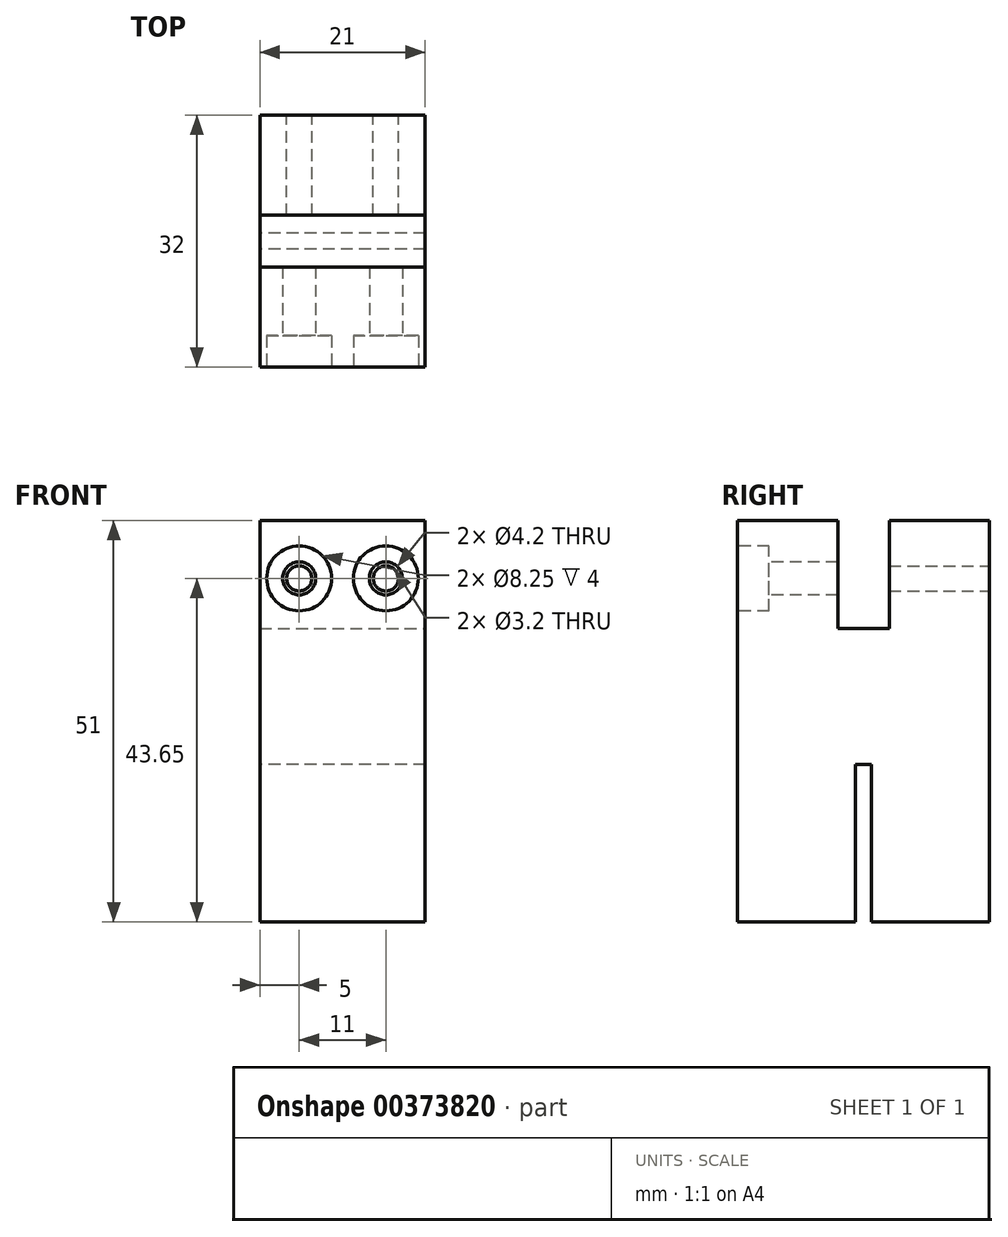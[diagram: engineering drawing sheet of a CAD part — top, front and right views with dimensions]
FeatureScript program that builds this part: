
annotation { "Feature Type Name" : "Feature", "Feature Type Description" : "" }
export const myFeature = defineFeature(function(context is Context, id is Id, definition is map)
    precondition{}
    {
        {
            var Q0;
            Q0=qCreatedBy(makeId("Right.planeOp"),FACE);
            var sketch = newSketch(context, id + "F0", { "sketchPlane" : qUnion([Q0])});
            skLineSegment(sketch, "E0.bottom", {"start": v(-16, -25) * mm, "end": v(16, -25) * mm});
            skLineSegment(sketch, "E0.top", {"start": v(-16, 25) * mm, "end": v(16, 25) * mm});
            skLineSegment(sketch, "E0.left", {"start": v(-16, -25) * mm, "end": v(-16, 25) * mm});
            skLineSegment(sketch, "E0.right", {"start": v(16, -25) * mm, "end": v(16, 25) * mm});
            skPoint(sketch, "E0.middle", {"position": v(0, 0) * mm});
            skLineSegment(sketch, "E1.bottom", {"start": v(-1, -5) * mm, "end": v(1, -5) * mm});
            skLineSegment(sketch, "E1.top", {"start": v(-1, -45) * mm, "end": v(1, -45) * mm});
            skLineSegment(sketch, "E1.left", {"start": v(-1, -5) * mm, "end": v(-1, -45) * mm});
            skLineSegment(sketch, "E1.right", {"start": v(1, -5) * mm, "end": v(1, -45) * mm});
            skPoint(sketch, "E1.middle", {"position": v(0, -25) * mm});
            skSolve(sketch);
        }
        {
            var Q0;
            Q0=makeQuery(id+"F0.imprint","IMPRINT",FACE,{"disambiguationData":[TD([[makeQuery(id+"F0.imprint","IMPRINT",EDGE,{"derivedFrom":sQuery(id+"F0.wireOp",EDGE,"E0.top")}),-1.0]])]});
            extrude(context, id + "F1", {"entities" : qUnion([Q0]), "depth" : 21 * mm});
        }
        {
            var Q0;
            Q0=makeQuery(id+"F1.opExtrude","SWEPT_FACE",FACE,{"disambiguationData":[OSD([sQuery(id+"F0.wireOp",EDGE,"E0.left")])]});
            var sketch = newSketch(context, id + "F2", { "sketchPlane" : qUnion([Q0])});
            skPoint(sketch, "E2", {"position": v(16, 18.65) * mm});
            skPoint(sketch, "E3", {"position": v(5, 18.65) * mm});
            skSolve(sketch);
        }
        {
            var Q0;
            Q0=makeQuery(id+"F1.opExtrude","CAP_FACE",FACE,{"disambiguationData":[OSD([sQuery(id+"F0.wireOp",EDGE,"E0.bottom"),sQuery(id+"F0.wireOp",EDGE,"E0.top"),sQuery(id+"F0.wireOp",EDGE,"E0.left"),sQuery(id+"F0.wireOp",EDGE,"E0.right"),sQuery(id+"F0.wireOp",EDGE,"E1.bottom"),sQuery(id+"F0.wireOp",EDGE,"E1.left"),sQuery(id+"F0.wireOp",EDGE,"E1.right")])],"isStart":false});
            var sketch = newSketch(context, id + "F3", { "sketchPlane" : qUnion([Q0])});
            skLineSegment(sketch, "E4.bottom", {"start": v(-3.28, 25) * mm, "end": v(3.27, 25) * mm});
            skLineSegment(sketch, "E4.top", {"start": v(-3.28, 12.3) * mm, "end": v(3.27, 12.3) * mm});
            skLineSegment(sketch, "E4.left", {"start": v(-3.28, 25) * mm, "end": v(-3.28, 12.3) * mm});
            skLineSegment(sketch, "E4.right", {"start": v(3.27, 25) * mm, "end": v(3.27, 12.3) * mm});
            skPoint(sketch, "E4.middle", {"position": v(0, 18.65) * mm});
            skPoint(sketch, "E4.middle.positionSnap0", {"position": v(0, 25) * mm});
            skPoint(sketch, "E4.centerSnap0", {"position": v(0, 25) * mm});
            skSolve(sketch);
        }
        {
            var Q0;
            Q0=makeQuery(id+"F3.imprint","IMPRINT",FACE,{"disambiguationData":[TD([[makeQuery(id+"F3.imprint","IMPRINT",EDGE,{"derivedFrom":sQuery(id+"F3.wireOp",EDGE,"E4.bottom")}),-1.0]])]});
            extrude(context, id + "F4", {"entities" : qUnion([Q0]), "operationType" : NewBodyOperationType.REMOVE, "endBound" : BoundingType.THROUGH_ALL, "oppositeDirection" : true, "depth" : 25 * mm});
        }
        {
            var Q0;
            Q0=sQuery(id+"F2.wireOp",VERTEX,"E3");
            var Q1;
            Q1=sQuery(id+"F2.wireOp",VERTEX,"E2");
            var Q2;
            Q2=makeQuery(id+"F1.opExtrude","SWEPT_BODY",BODY,{"disambiguationData":[OSD([sQuery(id+"F0.wireOp",EDGE,"E0.bottom"),sQuery(id+"F0.wireOp",EDGE,"E0.top"),sQuery(id+"F0.wireOp",EDGE,"E0.left"),sQuery(id+"F0.wireOp",EDGE,"E0.right"),sQuery(id+"F0.wireOp",EDGE,"E1.bottom"),sQuery(id+"F0.wireOp",EDGE,"E1.left"),sQuery(id+"F0.wireOp",EDGE,"E1.right")])]});
            hole(context, id + "F5", {"style" : HoleStyle.C_BORE, "endStyle" : HoleEndStyle.BLIND, "standardTappedOrClearance" : lookupTablePath({ "standard" : "ISO", "fit" : "Close", "size" : "M4", "type" : "Clearance" }), "standardBlindInLast" : lookupTablePath({ "fit" : "Close", "standard" : "ISO", "size" : "M4", "type" : "Clearance" }), "holeDiameter" : 4.2 * mm, "cBoreDiameter" : 8.25 * mm, "cBoreDepth" : 4 * mm, "holeDepth" : 14 * mm, "isTappedThrough" : true, "tappedDepth" : 2.4 * mm, "tapClearance" : 8, "startFromSketch" : true, "locations" : qUnion([Q0, Q1]), "scope" : qUnion([Q2])});
        }
        {
            var Q0;
            Q0=makeQuery(id+"F1.opExtrude","SWEPT_FACE",FACE,{"disambiguationData":[OSD([sQuery(id+"F0.wireOp",EDGE,"E0.right")])]});
            var sketch = newSketch(context, id + "F6", { "sketchPlane" : qUnion([Q0])});
            skLineSegment(sketch, "E5", {"start": v(-10.5, 25) * mm, "end": v(-10.5, 9.66) * mm});
            skPoint(sketch, "E6", {"position": v(-16, 18.65) * mm});
            skPoint(sketch, "E7.MirrorP", {"position": v(-5, 18.65) * mm});
            skSolve(sketch);
        }
        {
            var Q0;
            Q0=sQuery(id+"F6.wireOp",VERTEX,"E6");
            var Q1;
            Q1=sQuery(id+"F6.wireOp",VERTEX,"E7.MirrorP");
            var Q2;
            Q2=makeQuery(id+"F1.opExtrude","SWEPT_BODY",BODY,{"disambiguationData":[OSD([sQuery(id+"F0.wireOp",EDGE,"E0.bottom"),sQuery(id+"F0.wireOp",EDGE,"E0.top"),sQuery(id+"F0.wireOp",EDGE,"E0.left"),sQuery(id+"F0.wireOp",EDGE,"E0.right"),sQuery(id+"F0.wireOp",EDGE,"E1.bottom"),sQuery(id+"F0.wireOp",EDGE,"E1.left"),sQuery(id+"F0.wireOp",EDGE,"E1.right")])]});
            hole(context, id + "F7", {"style" : HoleStyle.SIMPLE, "endStyle" : HoleEndStyle.BLIND, "standardTappedOrClearance" : lookupTablePath({ "standard" : "ISO", "engagement" : "75%", "pitch" : "0.75 mm", "size" : "M4", "type" : "Tapped" }), "standardBlindInLast" : lookupTablePath({ "standard" : "ISO", "engagement" : "75%", "pitch" : "0.75 mm", "size" : "M4", "type" : "Tapped" }), "holeDiameter" : 3.2 * mm, "showTappedDepth" : true, "holeDepth" : 20 * mm, "isTappedThrough" : true, "tappedDepth" : 14 * mm, "tapClearance" : 8, "startFromSketch" : true, "locations" : qUnion([Q0, Q1]), "scope" : qUnion([Q2])});
        }
        {
            var Q0;
            {var subQ4=sQuery(id+"F0.wireOp",EDGE,"E0.left");var subQ5=sQuery(id+"F0.wireOp",EDGE,"E0.top");Q0=makeQuery(id+"F4.boolean.opBoolean","SPLIT",FACE,{"disambiguationData":[TD([makeQuery(id+"F1.opExtrude","SWEPT_FACE",FACE,{"disambiguationData":[OSD([subQ4])]})])],"derivedFrom":makeQuery(id+"F1.opExtrude","SWEPT_FACE",FACE,{"disambiguationData":[OSD([subQ5])]})});}
            var Q1;
            {var subQ3=sQuery(id+"F0.wireOp",EDGE,"E0.right");var subQ5=sQuery(id+"F0.wireOp",EDGE,"E0.top");Q1=makeQuery(id+"F4.boolean.opBoolean","SPLIT",FACE,{"disambiguationData":[TD([makeQuery(id+"F1.opExtrude","SWEPT_FACE",FACE,{"disambiguationData":[OSD([subQ3])]})])],"derivedFrom":makeQuery(id+"F1.opExtrude","SWEPT_FACE",FACE,{"disambiguationData":[OSD([subQ5])]})});}
            extrude(context, id + "F8", {"entities" : qUnion([Q0, Q1]), "operationType" : NewBodyOperationType.ADD, "depth" : 1 * mm});
        }
    });
